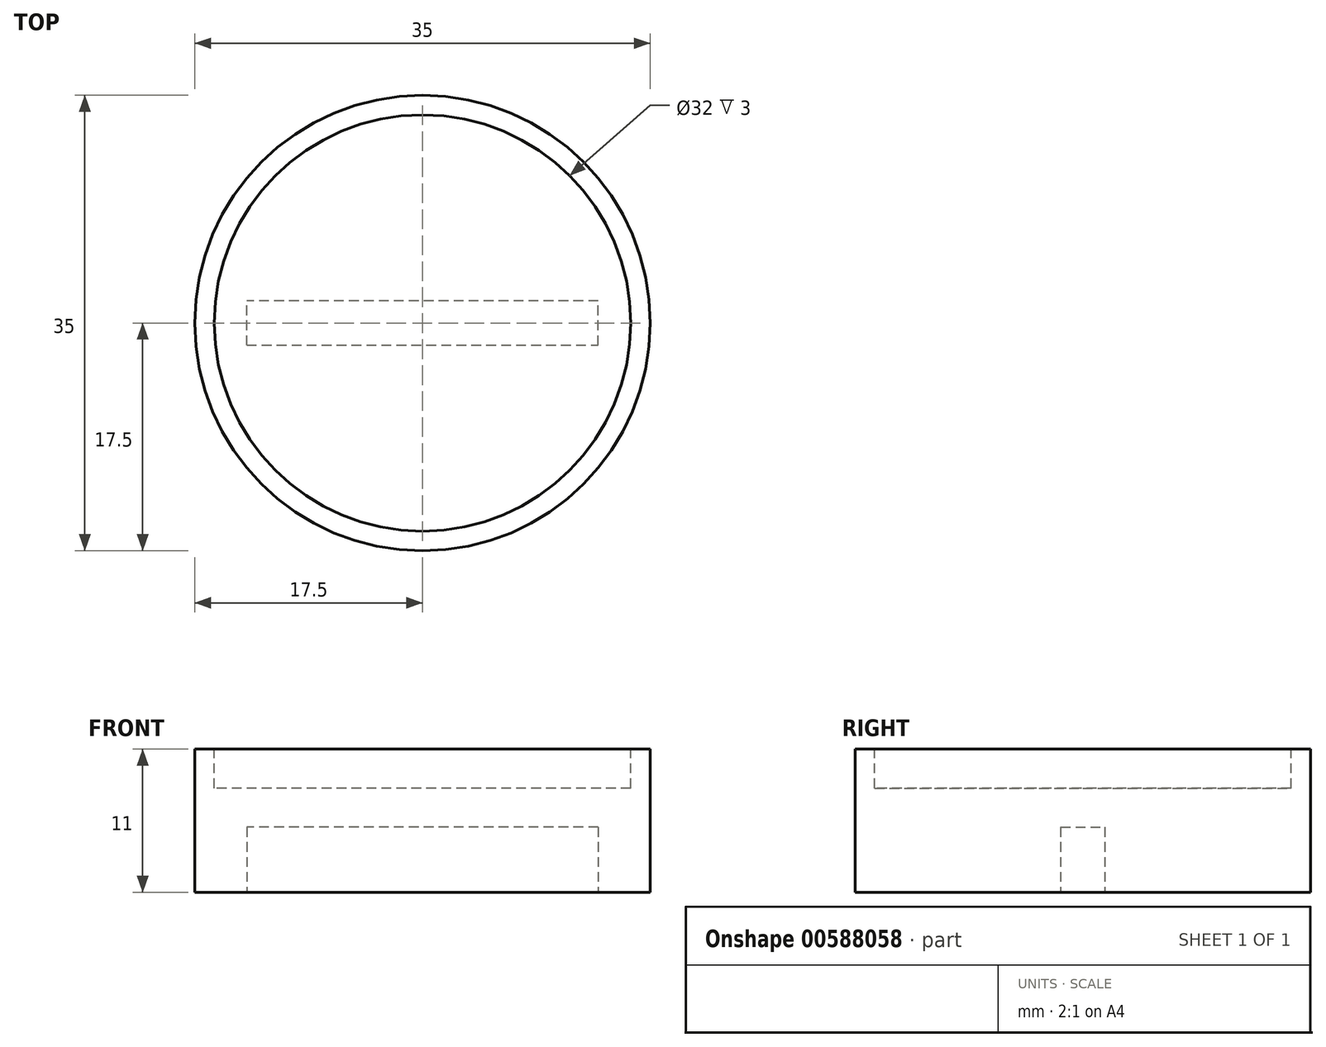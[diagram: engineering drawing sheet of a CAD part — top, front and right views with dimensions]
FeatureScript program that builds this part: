
annotation { "Feature Type Name" : "Feature", "Feature Type Description" : "" }
export const myFeature = defineFeature(function(context is Context, id is Id, definition is map)
    precondition{}
    {
        {
            var Q0;
            Q0=qCreatedBy(makeId("Top.planeOp"),FACE);
            var sketch = newSketch(context, id + "F0", { "sketchPlane" : qUnion([Q0])});
            skCircle(sketch, "E0", {"center": v(0, 0) * mm, "radius": 17.5 * mm});
            skSolve(sketch);
        }
        {
            var Q0;
            Q0 = qSketchRegion(id + "F0", true);
            extrude(context, id + "F1", {"entities" : qUnion([Q0]), "depth" : 11 * mm, "offsetDistance" : 25 * mm});
        }
        {
            var Q0;
            Q0=makeQuery(id+"F1.opExtrude","CAP_FACE",FACE,{"disambiguationData":[OSD([sQuery(id+"F0.wireOp",EDGE,"E0")])],"isStart":false});
            var sketch = newSketch(context, id + "F2", { "sketchPlane" : qUnion([Q0])});
            skCircle(sketch, "E1", {"center": v(0, 0) * mm, "radius": 16 * mm});
            skSolve(sketch);
        }
        {
            var Q0;
            Q0 = qSketchRegion(id + "F2", true);
            extrude(context, id + "F3", {"entities" : qUnion([Q0]), "operationType" : NewBodyOperationType.REMOVE, "oppositeDirection" : true, "depth" : 3 * mm, "offsetDistance" : 25 * mm});
        }
        {
            var Q0;
            Q0=makeQuery(id+"F1.opExtrude","CAP_FACE",FACE,{"disambiguationData":[OSD([sQuery(id+"F0.wireOp",EDGE,"E0")])],"isStart":true});
            var sketch = newSketch(context, id + "F4", { "sketchPlane" : qUnion([Q0])});
            skLineSegment(sketch, "E2.bottom", {"start": v(0, 0) * mm, "end": v(13.5, 0) * mm});
            skLineSegment(sketch, "E2.top", {"start": v(0, 1.7) * mm, "end": v(13.5, 1.7) * mm});
            skLineSegment(sketch, "E2.left", {"start": v(0, 0) * mm, "end": v(0, 1.7) * mm});
            skLineSegment(sketch, "E2.right", {"start": v(13.5, 0) * mm, "end": v(13.5, 1.7) * mm});
            skLineSegment(sketch, "E3.bottom", {"start": v(0, 0) * mm, "end": v(-13.5, 0) * mm});
            skLineSegment(sketch, "E3.top", {"start": v(0, 1.7) * mm, "end": v(-13.5, 1.7) * mm});
            skLineSegment(sketch, "E3.right", {"start": v(-13.5, 0) * mm, "end": v(-13.5, 1.7) * mm});
            skLineSegment(sketch, "E4.top", {"start": v(0, -1.7) * mm, "end": v(13.5, -1.7) * mm});
            skLineSegment(sketch, "E4.left", {"start": v(0, 0) * mm, "end": v(0, -1.7) * mm});
            skLineSegment(sketch, "E4.right", {"start": v(13.5, 0) * mm, "end": v(13.5, -1.7) * mm});
            skLineSegment(sketch, "E5.top", {"start": v(0, -1.7) * mm, "end": v(-13.5, -1.7) * mm});
            skLineSegment(sketch, "E5.right", {"start": v(-13.5, 0) * mm, "end": v(-13.5, -1.7) * mm});
            skLineSegment(sketch, "E6.bottom", {"start": v(0, -1.7) * mm, "end": v(1.7, -1.7) * mm});
            skLineSegment(sketch, "E6.top", {"start": v(0, -17.7) * mm, "end": v(1.7, -17.7) * mm});
            skLineSegment(sketch, "E6.left", {"start": v(0, -1.7) * mm, "end": v(0, -17.7) * mm});
            skLineSegment(sketch, "E6.right", {"start": v(1.7, -1.7) * mm, "end": v(1.7, -17.7) * mm});
            skLineSegment(sketch, "E7.bottom", {"start": v(0, -1.7) * mm, "end": v(-1.7, -1.7) * mm});
            skLineSegment(sketch, "E7.top", {"start": v(0, -17.7) * mm, "end": v(-1.7, -17.7) * mm});
            skLineSegment(sketch, "E7.right", {"start": v(-1.7, -1.7) * mm, "end": v(-1.7, -17.7) * mm});
            skLineSegment(sketch, "E8.bottom", {"start": v(-1.7, -1.7) * mm, "end": v(-5.1, -1.7) * mm});
            skLineSegment(sketch, "E8.top", {"start": v(-1.7, -17.7) * mm, "end": v(-5.1, -17.7) * mm});
            skLineSegment(sketch, "E8.right", {"start": v(-5.1, -1.7) * mm, "end": v(-5.1, -17.7) * mm});
            skSolve(sketch);
        }
        {
            var Q0;
            {var subQ0=sQuery(id+"F4.wireOp",EDGE,"E8.bottom");Q0=makeQuery(id+"F4.imprint","IMPRINT",FACE,{"disambiguationData":[TD([[makeQuery(id+"F4.imprint","IMPRINT",EDGE,{"derivedFrom":subQ0}),1.0]])]});}
            var Q1;
            Q1=makeQuery(id+"F4.imprint","IMPRINT",FACE,{"disambiguationData":[TD([[makeQuery(id+"F4.imprint","IMPRINT",EDGE,{"derivedFrom":sQuery(id+"F4.wireOp",EDGE,"E3.bottom")}),1.0]])]});
            var Q2;
            Q2=makeQuery(id+"F4.imprint","IMPRINT",FACE,{"disambiguationData":[TD([[makeQuery(id+"F4.imprint","IMPRINT",EDGE,{"derivedFrom":sQuery(id+"F4.wireOp",EDGE,"E2.bottom")}),-1.0]])]});
            var Q3;
            Q3=makeQuery(id+"F4.imprint","IMPRINT",FACE,{"disambiguationData":[TD([[makeQuery(id+"F4.imprint","IMPRINT",EDGE,{"derivedFrom":sQuery(id+"F4.wireOp",EDGE,"E2.top")}),-1.0]])]});
            var Q4;
            Q4=makeQuery(id+"F4.imprint","IMPRINT",FACE,{"disambiguationData":[TD([[makeQuery(id+"F4.imprint","IMPRINT",EDGE,{"derivedFrom":sQuery(id+"F4.wireOp",EDGE,"E3.top")}),1.0]])]});
            extrude(context, id + "F5", {"entities" : qUnion([Q0, Q1, Q2, Q3, Q4]), "operationType" : NewBodyOperationType.REMOVE, "oppositeDirection" : true, "depth" : 5 * mm, "offsetDistance" : 25 * mm});
        }
    });
